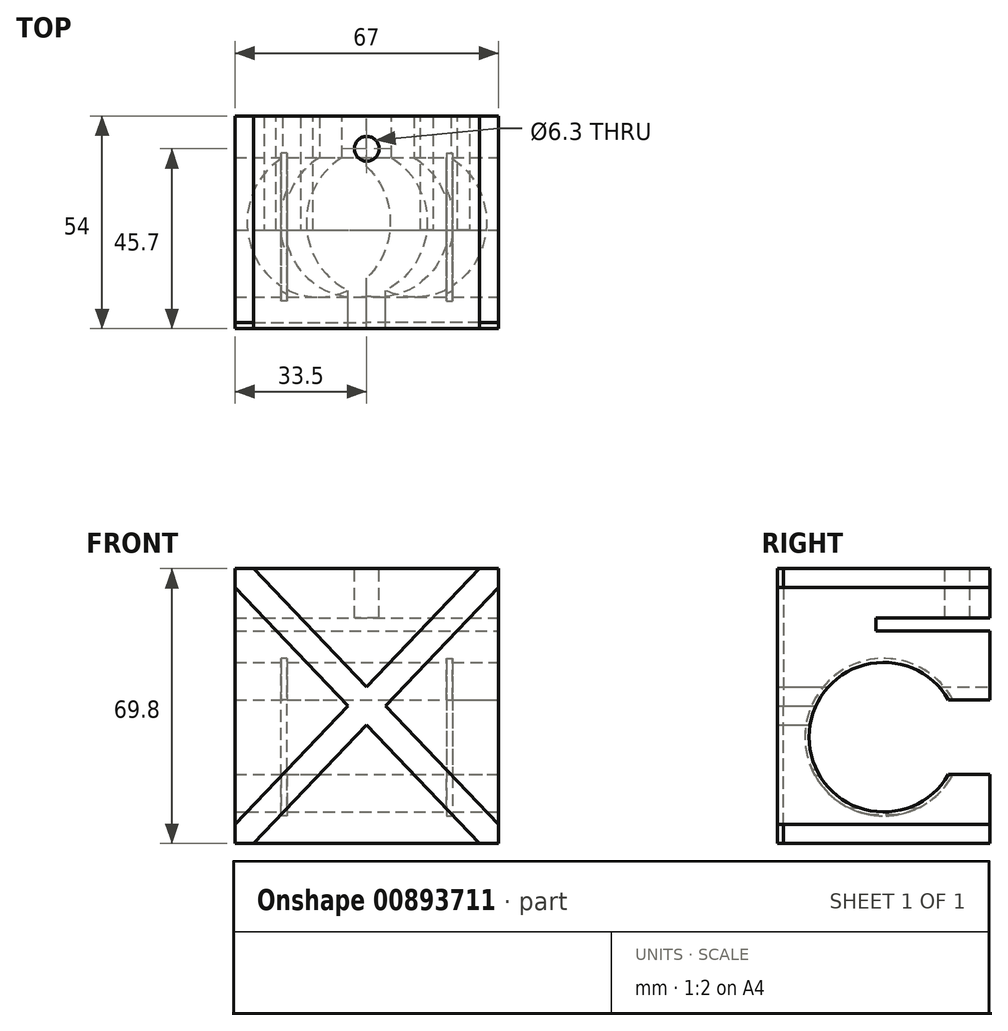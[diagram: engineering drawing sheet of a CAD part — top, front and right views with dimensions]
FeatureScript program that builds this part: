
annotation { "Feature Type Name" : "Feature", "Feature Type Description" : "" }
export const myFeature = defineFeature(function(context is Context, id is Id, definition is map)
    precondition{}
    {
        {
            var Q0;
            Q0=qCreatedBy(makeId("Front.planeOp"),FACE);
            var sketch = newSketch(context, id + "F0", { "sketchPlane" : qUnion([Q0])});
            skLineSegment(sketch, "E0.bottom", {"start": v(33.5, 34.9) * mm, "end": v(-33.5, 34.9) * mm});
            skLineSegment(sketch, "E0.top", {"start": v(33.5, -34.9) * mm, "end": v(-33.5, -34.9) * mm});
            skLineSegment(sketch, "E0.left", {"start": v(33.5, 34.9) * mm, "end": v(33.5, -34.9) * mm});
            skLineSegment(sketch, "E0.right", {"start": v(-33.5, 34.9) * mm, "end": v(-33.5, -34.9) * mm});
            skPoint(sketch, "E0.middle", {"position": v(0, 0) * mm});
            skLineSegment(sketch, "E1", {"start": v(33.5, -30.1) * mm, "end": v(4.79, 0) * mm});
            skLineSegment(sketch, "E2", {"start": v(28.7, -34.9) * mm, "end": v(0, -4.81) * mm});
            skLineSegment(sketch, "E3", {"start": v(-28.7, -34.9) * mm, "end": v(0, -4.81) * mm});
            skLineSegment(sketch, "E4", {"start": v(-33.5, -30.1) * mm, "end": v(-4.79, 0) * mm});
            skLineSegment(sketch, "E5", {"start": v(-33.5, 30.1) * mm, "end": v(-4.79, 0) * mm});
            skLineSegment(sketch, "E6", {"start": v(-28.7, 34.9) * mm, "end": v(0, 4.81) * mm});
            skLineSegment(sketch, "E7", {"start": v(28.7, 34.9) * mm, "end": v(0, 4.81) * mm});
            skLineSegment(sketch, "E8", {"start": v(33.5, 30.1) * mm, "end": v(4.79, 0) * mm});
            skSolve(sketch);
        }
        {
            var Q0;
            {var subQ0=sQuery(id+"F0.wireOp",EDGE,"E4");Q0=makeQuery(id+"F0.imprint","IMPRINT",FACE,{"disambiguationData":[TD([[makeQuery(id+"F0.imprint","IMPRINT",EDGE,{"derivedFrom":subQ0}),1.0]])]});}
            var Q1;
            {var subQ0=sQuery(id+"F0.wireOp",EDGE,"E6");Q1=makeQuery(id+"F0.imprint","IMPRINT",FACE,{"disambiguationData":[TD([[makeQuery(id+"F0.imprint","IMPRINT",EDGE,{"derivedFrom":subQ0}),1.0]])]});}
            var Q2;
            {var subQ0=sQuery(id+"F0.wireOp",EDGE,"E1");Q2=makeQuery(id+"F0.imprint","IMPRINT",FACE,{"disambiguationData":[TD([[makeQuery(id+"F0.imprint","IMPRINT",EDGE,{"derivedFrom":subQ0}),-1.0]])]});}
            var Q3;
            {var subQ0=sQuery(id+"F0.wireOp",EDGE,"E2");Q3=makeQuery(id+"F0.imprint","IMPRINT",FACE,{"disambiguationData":[TD([[makeQuery(id+"F0.imprint","IMPRINT",EDGE,{"derivedFrom":subQ0}),1.0]])]});}
            extrude(context, id + "F1", {"entities" : qUnion([Q0, Q1, Q2, Q3]), "depth" : 54 * mm, "offsetDistance" : 25 * mm});
        }
        {
            var Q0;
            {var subQ0=sQuery(id+"F0.wireOp",EDGE,"E1");Q0=makeQuery(id+"F0.imprint","IMPRINT",FACE,{"disambiguationData":[TD([[makeQuery(id+"F0.imprint","IMPRINT",EDGE,{"derivedFrom":subQ0}),1.0]])]});}
            extrude(context, id + "F2", {"entities" : qUnion([Q0]), "depth" : 52.5 * mm, "offsetDistance" : 25 * mm});
        }
        {
            var Q0;
            Q0=makeQuery(id+"F1.opExtrude","SWEPT_FACE",FACE,{"disambiguationData":[OSD([sQuery(id+"F0.wireOp",EDGE,"E0.left")])]});
            cPlane(context, id + "F3", {"entities" : qUnion([Q0]), "cplaneType" : CPlaneType.OFFSET, "offset" : 0 * mm, "width" : 150 * mm, "height" : 150 * mm});
        }
        {
            var Q0;
            Q0=qCreatedBy(id+"F3.planeOp",FACE);
            var sketch = newSketch(context, id + "F4", { "sketchPlane" : qUnion([Q0])});
            skCircle(sketch, "E9", {"center": v(-27, -7.9) * mm, "radius": 19 * mm});
            skLineSegment(sketch, "E10", {"start": v(0, 22.4) * mm, "end": v(-29, 22.4) * mm});
            skLineSegment(sketch, "E11", {"start": v(-29, 22.4) * mm, "end": v(-29, 19.1) * mm});
            skLineSegment(sketch, "E12", {"start": v(-29, 19.1) * mm, "end": v(0, 19.1) * mm});
            skLineSegment(sketch, "E13", {"start": v(-10.55, 1.6) * mm, "end": v(0, 1.6) * mm});
            skLineSegment(sketch, "E14", {"start": v(-10.55, -17.4) * mm, "end": v(0, -17.4) * mm});
            skLineSegment(sketch, "E15", {"start": v(0, 1.6) * mm, "end": v(0, -17.4) * mm});
            skLineSegment(sketch, "E16", {"start": v(0, 19.1) * mm, "end": v(0, 22.4) * mm});
            skSolve(sketch);
        }
        {
            var Q0;
            Q0=makeQuery(id+"F4.imprint","IMPRINT",FACE,{"disambiguationData":[TD([[makeQuery(id+"F4.imprint","IMPRINT",EDGE,{"derivedFrom":sQuery(id+"F4.wireOp",EDGE,"E10")}),1.0]])]});
            var Q1;
            {var subQ0=sQuery(id+"F4.wireOp",EDGE,"E9");var subQ1=makeQuery(id+"F4.imprint","INTERSECT",VERTEX,{"derivedFrom":[subQ0,sQuery(id+"F4.wireOp",EDGE,"E13")]});Q1=makeQuery(id+"F4.imprint","IMPRINT",FACE,{"disambiguationData":[TD([[makeQuery(id+"F4.imprint","IMPRINT",EDGE,{"disambiguationData":[TD([[subQ1,-1.0]])],"derivedFrom":subQ0}),1.0]])]});}
            var Q2;
            {var subQ0=sQuery(id+"F4.wireOp",EDGE,"E13");Q2=makeQuery(id+"F4.imprint","IMPRINT",FACE,{"disambiguationData":[TD([[makeQuery(id+"F4.imprint","IMPRINT",EDGE,{"derivedFrom":subQ0}),-1.0]])]});}
            extrude(context, id + "F5", {"entities" : qUnion([Q0, Q1, Q2]), "operationType" : NewBodyOperationType.REMOVE, "oppositeDirection" : true, "depth" : 67 * mm, "offsetDistance" : 25 * mm});
        }
        {
            var Q0;
            Q0=makeQuery(id+"F1.opExtrude","SWEPT_FACE",FACE,{"disambiguationData":[OSD([sQuery(id+"F0.wireOp",EDGE,"E0.bottom")])]});
            cPlane(context, id + "F6", {"entities" : qUnion([Q0]), "cplaneType" : CPlaneType.OFFSET, "offset" : 0 * mm, "width" : 150 * mm, "height" : 150 * mm});
        }
        {
            var Q0;
            Q0=qCreatedBy(id+"F6.planeOp",FACE);
            var sketch = newSketch(context, id + "F7", { "sketchPlane" : qUnion([Q0])});
            skCircle(sketch, "E17", {"center": v(0, -8.3) * mm, "radius": 3.15 * mm});
            skSolve(sketch);
        }
        {
            var Q0;
            Q0=makeQuery(id+"F7.imprint","IMPRINT",FACE,{"disambiguationData":[TD([[makeQuery(id+"F7.imprint","IMPRINT",EDGE,{"derivedFrom":sQuery(id+"F7.wireOp",EDGE,"E17")}),1.0]])]});
            extrude(context, id + "F8", {"entities" : qUnion([Q0]), "operationType" : NewBodyOperationType.REMOVE, "oppositeDirection" : true, "depth" : 12.5 * mm, "offsetDistance" : 25 * mm});
        }
        {
            var Q0;
            Q0=makeQuery(id+"F1.opExtrude","SWEPT_FACE",FACE,{"disambiguationData":[OSD([sQuery(id+"F0.wireOp",EDGE,"E0.left")])]});
            cPlane(context, id + "F9", {"entities" : qUnion([Q0]), "cplaneType" : CPlaneType.OFFSET, "offset" : 12.5 * mm, "oppositeDirection" : true, "width" : 150 * mm, "height" : 150 * mm});
        }
        {
            var Q0;
            Q0=qCreatedBy(id+"F9.planeOp",FACE);
            var sketch = newSketch(context, id + "F10", { "sketchPlane" : qUnion([Q0])});
            skCircle(sketch, "E18", {"center": v(-27, -7.9) * mm, "radius": 20 * mm});
            skSolve(sketch);
        }
        {
            var Q0;
            Q0=makeQuery(id+"F10.imprint","IMPRINT",FACE,{"disambiguationData":[TD([[makeQuery(id+"F10.imprint","IMPRINT",EDGE,{"derivedFrom":sQuery(id+"F10.wireOp",EDGE,"E18")}),1.0]])]});
            extrude(context, id + "F11", {"entities" : qUnion([Q0]), "operationType" : NewBodyOperationType.REMOVE, "endBound" : BoundingType.SYMMETRIC, "oppositeDirection" : true, "depth" : 1.5 * mm, "offsetDistance" : 25 * mm});
        }
        {
            var Q0;
            Q0=makeQuery(id+"F1.opExtrude","SWEPT_FACE",FACE,{"disambiguationData":[OSD([sQuery(id+"F0.wireOp",EDGE,"E0.right")])]});
            cPlane(context, id + "F12", {"entities" : qUnion([Q0]), "cplaneType" : CPlaneType.OFFSET, "offset" : 12.5 * mm, "oppositeDirection" : true, "width" : 150 * mm, "height" : 150 * mm});
        }
        {
            var Q0;
            Q0=qCreatedBy(id+"F12.planeOp",FACE);
            var sketch = newSketch(context, id + "F13", { "sketchPlane" : qUnion([Q0])});
            skCircle(sketch, "E19", {"center": v(27, -7.9) * mm, "radius": 20 * mm});
            skSolve(sketch);
        }
        {
            var Q0;
            Q0=makeQuery(id+"F13.imprint","IMPRINT",FACE,{"disambiguationData":[TD([[makeQuery(id+"F13.imprint","IMPRINT",EDGE,{"derivedFrom":sQuery(id+"F13.wireOp",EDGE,"E19")}),1.0]])]});
            extrude(context, id + "F14", {"entities" : qUnion([Q0]), "operationType" : NewBodyOperationType.REMOVE, "endBound" : BoundingType.SYMMETRIC, "oppositeDirection" : true, "depth" : 1.5 * mm, "offsetDistance" : 25 * mm});
        }
    });
